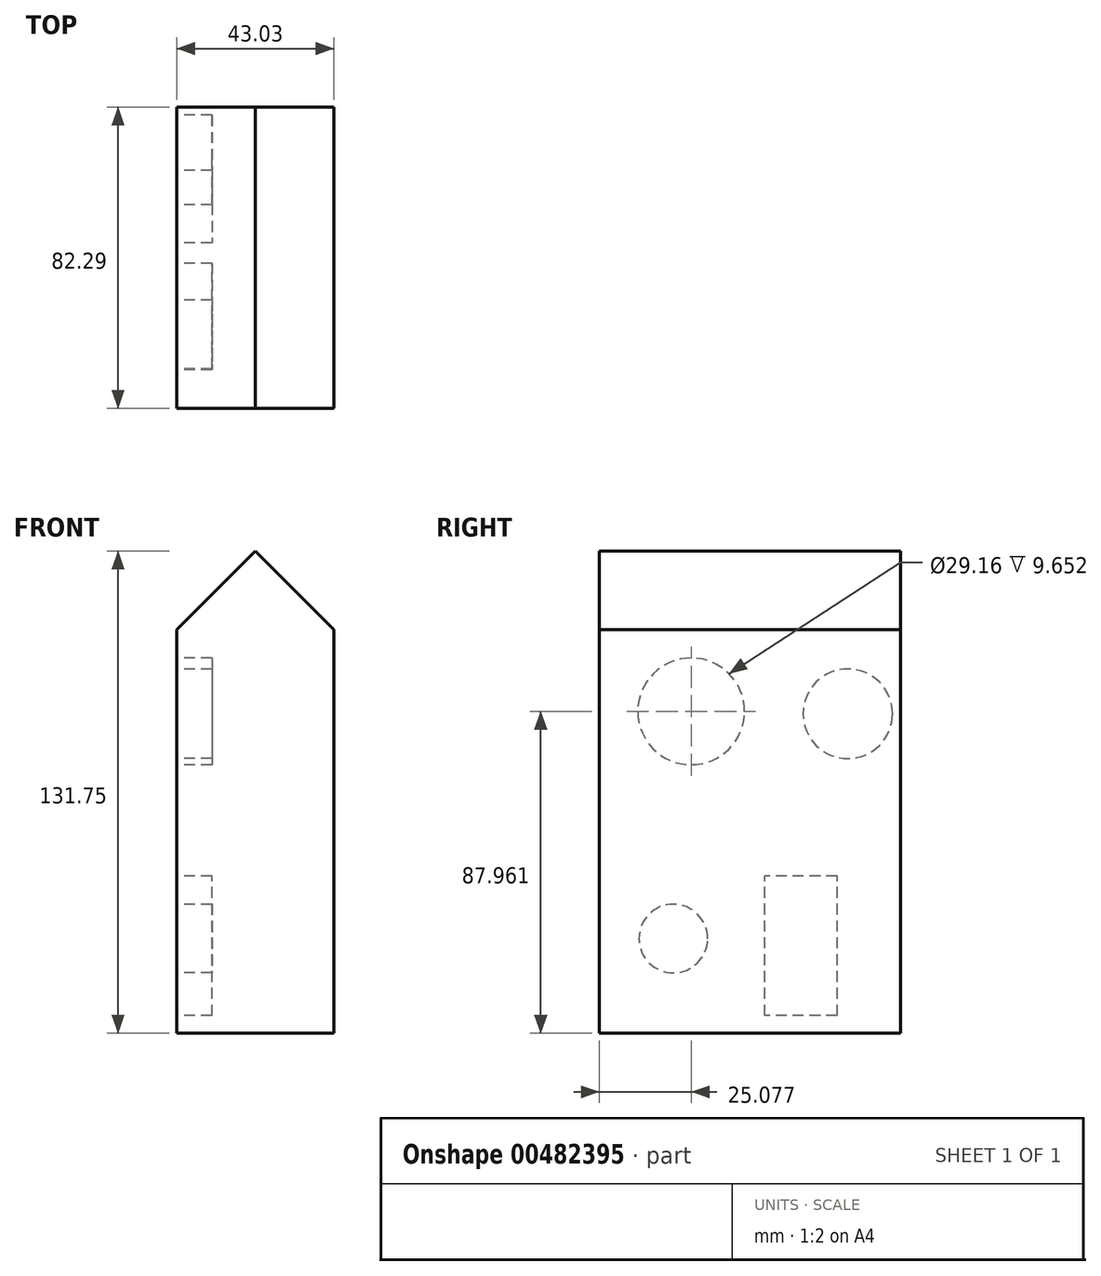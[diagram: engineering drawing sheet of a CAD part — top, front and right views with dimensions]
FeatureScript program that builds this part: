
annotation { "Feature Type Name" : "Feature", "Feature Type Description" : "" }
export const myFeature = defineFeature(function(context is Context, id is Id, definition is map)
    precondition{}
    {
        {
            var Q0;
            Q0=qCreatedBy(makeId("Top.planeOp"),FACE);
            var sketch = newSketch(context, id + "F0", { "sketchPlane" : qUnion([Q0])});
            skLineSegment(sketch, "E0.bottom", {"start": v(-131.76, 66.08) * mm, "end": v(-88.73, 66.08) * mm});
            skLineSegment(sketch, "E0.top", {"start": v(-131.76, -16.21) * mm, "end": v(-88.73, -16.21) * mm});
            skLineSegment(sketch, "E0.left", {"start": v(-131.76, 66.08) * mm, "end": v(-131.76, -16.21) * mm});
            skLineSegment(sketch, "E0.right", {"start": v(-88.73, 66.08) * mm, "end": v(-88.73, -16.21) * mm});
            skSolve(sketch);
        }
        {
            var Q0;
            Q0 = qSketchRegion(id + "F0", true);
            extrude(context, id + "F1", {"entities" : qUnion([Q0]), "depth" : 135.64 * mm});
        }
        {
            var Q0;
            Q0=makeQuery(id+"F1.opExtrude","CAP_EDGE",EDGE,{"disambiguationData":[OSD([sQuery(id+"F0.wireOp",EDGE,"E0.left")])],"isStart":false});
            var Q1;
            Q1=makeQuery(id+"F1.opExtrude","CAP_EDGE",EDGE,{"disambiguationData":[OSD([sQuery(id+"F0.wireOp",EDGE,"E0.right")])],"isStart":false});
            chamfer(context, id + "F2", {"entities" : qUnion([Q0, Q1]), "width" : 25.4 * mm, "tangentPropagation" : true});
        }
        {
            var Q0;
            Q0=makeQuery(id+"F1.opExtrude","SWEPT_FACE",FACE,{"disambiguationData":[OSD([sQuery(id+"F0.wireOp",EDGE,"E0.left")])]});
            var sketch = newSketch(context, id + "F3", { "sketchPlane" : qUnion([Q0])});
            skLineSegment(sketch, "E1.bottom", {"start": v(-48.77, 4.83) * mm, "end": v(-29.04, 4.83) * mm});
            skLineSegment(sketch, "E1.top", {"start": v(-48.77, 42.96) * mm, "end": v(-29.04, 42.96) * mm});
            skLineSegment(sketch, "E1.left", {"start": v(-48.77, 4.83) * mm, "end": v(-48.77, 42.96) * mm});
            skLineSegment(sketch, "E1.right", {"start": v(-29.04, 4.83) * mm, "end": v(-29.04, 42.96) * mm});
            skCircle(sketch, "E2", {"center": v(-51.65, 87.3) * mm, "radius": 12.22 * mm});
            skCircle(sketch, "E3", {"center": v(-8.87, 87.96) * mm, "radius": 14.58 * mm});
            skCircle(sketch, "E4", {"center": v(-4, 25.9) * mm, "radius": 9.38 * mm});
            skSolve(sketch);
        }
        {
            var Q0;
            Q0 = qSketchRegion(id + "F3", true);
            extrude(context, id + "F4", {"entities" : qUnion([Q0]), "operationType" : NewBodyOperationType.REMOVE, "oppositeDirection" : true, "depth" : 9.65 * mm});
        }
    });
